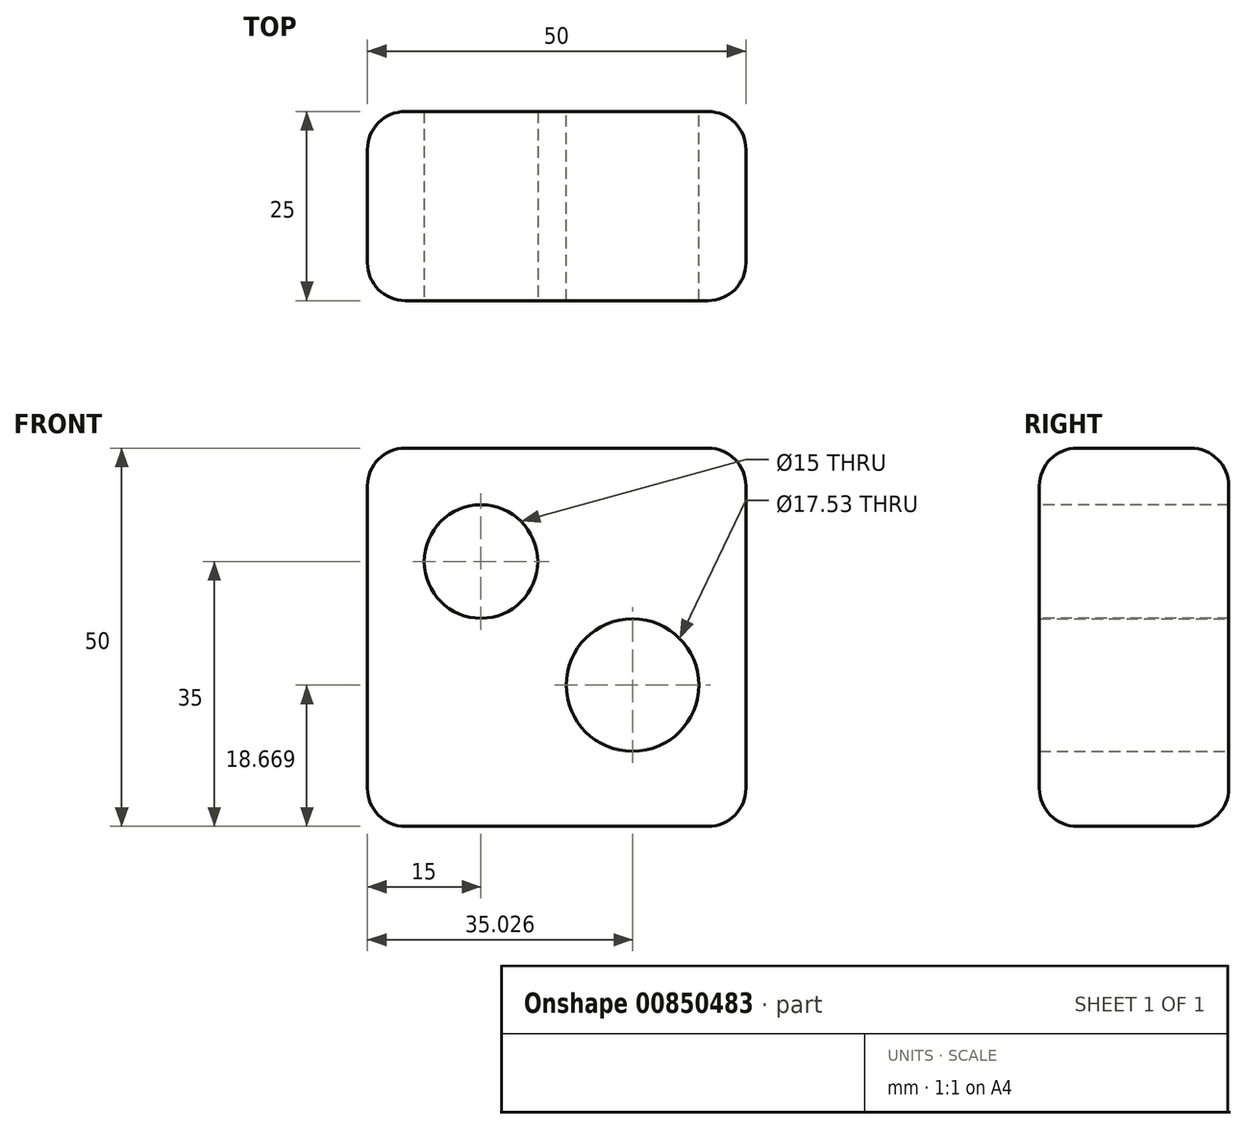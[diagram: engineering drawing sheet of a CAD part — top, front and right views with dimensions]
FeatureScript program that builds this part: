
annotation { "Feature Type Name" : "Feature", "Feature Type Description" : "" }
export const myFeature = defineFeature(function(context is Context, id is Id, definition is map)
    precondition{}
    {
        {
            var Q0;
            Q0=qCreatedBy(makeId("Front.planeOp"),FACE);
            var sketch = newSketch(context, id + "F0", { "sketchPlane" : qUnion([Q0])});
            skLineSegment(sketch, "E0.bottom", {"start": v(0, 0) * mm, "end": v(50, 0) * mm});
            skLineSegment(sketch, "E0.top", {"start": v(0, 50) * mm, "end": v(50, 50) * mm});
            skLineSegment(sketch, "E0.left", {"start": v(0, 0) * mm, "end": v(0, 50) * mm});
            skLineSegment(sketch, "E0.right", {"start": v(50, 0) * mm, "end": v(50, 50) * mm});
            skSolve(sketch);
        }
        {
            var Q0;
            Q0 = qSketchRegion(id + "F0", true);
            extrude(context, id + "F1", {"entities" : qUnion([Q0]), "depth" : 25 * mm, "offsetDistance" : 25 * mm});
        }
        {
            var Q0;
            Q0=makeQuery(id+"F1.opExtrude","CAP_FACE",FACE,{"disambiguationData":[OSD([sQuery(id+"F0.wireOp",EDGE,"E0.bottom"),sQuery(id+"F0.wireOp",EDGE,"E0.top"),sQuery(id+"F0.wireOp",EDGE,"E0.left"),sQuery(id+"F0.wireOp",EDGE,"E0.right")])],"isStart":false});
            var sketch = newSketch(context, id + "F2", { "sketchPlane" : qUnion([Q0])});
            skCircle(sketch, "E1", {"center": v(15, 35) * mm, "radius": 7.5 * mm});
            skSolve(sketch);
        }
        {
            var Q0;
            Q0 = qSketchRegion(id + "F2", true);
            extrude(context, id + "F3", {"entities" : qUnion([Q0]), "operationType" : NewBodyOperationType.REMOVE, "oppositeDirection" : true, "depth" : 25 * mm, "offsetDistance" : 25 * mm});
        }
        {
            var Q0;
            Q0=makeQuery(id+"F1.opExtrude","SWEPT_FACE",FACE,{"disambiguationData":[OSD([sQuery(id+"F0.wireOp",EDGE,"E0.left")])]});
            var Q1;
            Q1=makeQuery(id+"F1.opExtrude","SWEPT_FACE",FACE,{"disambiguationData":[OSD([sQuery(id+"F0.wireOp",EDGE,"E0.top")])]});
            var Q2;
            Q2=makeQuery(id+"F1.opExtrude","SWEPT_FACE",FACE,{"disambiguationData":[OSD([sQuery(id+"F0.wireOp",EDGE,"E0.right")])]});
            var Q3;
            Q3=makeQuery(id+"F1.opExtrude","SWEPT_FACE",FACE,{"disambiguationData":[OSD([sQuery(id+"F0.wireOp",EDGE,"E0.bottom")])]});
            fillet(context, id + "F4", {"entities" : qUnion([Q0, Q1, Q2, Q3]), "radius" : 5 * mm, "tangentPropagation" : true, "allowEdgeOverflow" : false});
        }
        {
            var Q0;
            Q0=makeQuery(id+"F1.opExtrude","CAP_FACE",FACE,{"disambiguationData":[OSD([sQuery(id+"F0.wireOp",EDGE,"E0.bottom"),sQuery(id+"F0.wireOp",EDGE,"E0.top"),sQuery(id+"F0.wireOp",EDGE,"E0.left"),sQuery(id+"F0.wireOp",EDGE,"E0.right")])],"isStart":true});
            var sketch = newSketch(context, id + "F5", { "sketchPlane" : qUnion([Q0])});
            skCircle(sketch, "E2", {"center": v(-35.03, 18.67) * mm, "radius": 8.76 * mm});
            skSolve(sketch);
        }
        {
            var Q0;
            Q0=makeQuery(id+"F5.imprint","IMPRINT",FACE,{"disambiguationData":[TD([[makeQuery(id+"F5.imprint","IMPRINT",EDGE,{"derivedFrom":sQuery(id+"F5.wireOp",EDGE,"E2")}),1.0]])]});
            var Q1;
            Q1=makeQuery(id+"F1.opExtrude","CAP_FACE",FACE,{"disambiguationData":[OSD([sQuery(id+"F0.wireOp",EDGE,"E0.bottom"),sQuery(id+"F0.wireOp",EDGE,"E0.top"),sQuery(id+"F0.wireOp",EDGE,"E0.left"),sQuery(id+"F0.wireOp",EDGE,"E0.right")])],"isStart":false});
            extrude(context, id + "F6", {"entities" : qUnion([Q0]), "operationType" : NewBodyOperationType.REMOVE, "endBound" : BoundingType.THROUGH_ALL, "oppositeDirection" : true, "depth" : 25 * mm, "endBoundEntityFace" : qUnion([Q1]), "hasOffset" : true, "offsetDistance" : 25 * mm});
        }
    });
